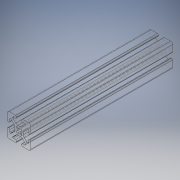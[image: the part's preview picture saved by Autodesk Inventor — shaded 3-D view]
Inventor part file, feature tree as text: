
AUTODESK INVENTOR PART (.ipt)
format: ipt  version: 2019 (Build 230136000, 136)  size: 237,568 bytes
history: native  units: in
note: dims shown in document units (in); Inventor stores cm internally (conversion verified against a paired STEP export)
features: plane x1, extrude x1, sketch x1
ambient origin geometry x8: Origin, YZ Plane, XZ Plane, XY Plane, X Axis, Y Axis, Z Axis, Center Point
bodies: Solid1 (feature_tree)
feature tree (3):
  plane  "Work Plane1"
  extrude  "Extrusion1"  [1 undecoded]
  sketch  "Sketch1"  dims[d0=9.0in d1=0.0in]
note: 1 required parameter value undecoded (feature->parameter linkage not recoverable at this tier; creation-order binding heuristic only, values carry confidence <= 0.55)
